# Revit family: Faucets-Commercial_TEL3LG10_TOTO
name_source: partatom
category: Plumbing Fixtures
revit_build: Autodesk Revit Architecture 2013 (Build: 20130531_2115(x64)
units: mm (PartAtom-declared; Revit-internal decimal feet)

## types (1)
- TEL3LG10
    04 CSI = 22 42 39
    95 CSI = 15416
    ADA Compliant = Yes
    Apparent Power = 0 VA
    Assembly Code = D2010
    CAD Drawing URL = http://assets.totousa.com
    CWFU = 0
    Color Availability = #CP Polished Chrome
    Current = 0 A
    Depth = 0"
    Description = Faucets, Commercial, Gooseneck EcoPower Faucet, 0.5 GPM - Single Supply
    Finish = Metal - TOTO - Chrome - Polished
    Flow Pressure = 0.00 psi
    Flow Rate = 1 GPM
    Frequency = 0 Hz
    Height = 5 7/8"
    Hot Water Connection NPT Radius = 0"
    Industry Standards = Exceeds mandatory baseline, 0.20 gallon/cycle, of California Green Building Code, CALGreen,Meets or exceeds ASME A112.18.1/CSA B125.1, NSF 61-9, and ASSE 1070*,Certifi cations: IAPMO(cUPC), ASSE, State of Massachusetts, and others,Code Compliance: UPC, IPC, NSPC, NPC Canada, and others,Legislative compliance: California AB 1953 & Vermont S.152, and City of Los Angeles Water Effi ciency Ordinance,ADA compliant
    Manufacturer = TOTO USA, Inc.
    Manufacturer Fax = (770) 282-0002
    Method of Operation = Hydropower self-generating system
    Model = TEL3LG10
    Mount Type = Single-hole mount
    Number of Poles = 1
    Product Line = Gooseneck EcoPower Faucet, 0.5 GPM - Single Supply
    Sensor Activation Time = Automatically turns OFF when user removes hands Maximum continuous run time is 10 or 60 seconds
    Sensor Detection Range = Factory set at 2-1/4" Faucet automatically sets the detection range according to the size of the basin
    Sensor Detection Time = ON feature: Immediate OFF feature: 1 second delay
    Shipping Weight = 0.00 kip
    Sink Holes Applications = Single Supply
    Spec Sheet URL = http://assets.totousa.com
    Style = Commercial
    Subcategory = Faucets
    Toto BIM Number = BM-00249
    URL = http://www.totousa.com
    Voltage = 0 V
    Warranty = Three Year Limited Warranty
    Warranty URL = http://www.totousa.com
    Waste Connection Radius = 0"
    Water Connection Radius = 1/4"
    Width = 0"

## geometry (parser evidence)
native form markers: Blend x24, Sweep x3
no freeform markers — native parametric forms only
